# Revit family: 3000.123.6-124.6 Down Pipe Junction 100x100 SE
name_source: partatom
category: Plumbing Fixtures
units: mm (PartAtom-declared; Revit-internal decimal feet)

## family parameters
Always vertical = Yes
Cut with Voids When Loaded = No
OmniClass Number = 23.13.41.39
Part Type = Normal
Room Calculation Point = No
Round Connector Dimension = Use Diameter
Shared = No
Work Plane-Based = No

## types (2) — shared parameters
CW Connection = No
HW Connection = No
Manufacturer = Aquanight Industries Ltd
URL = www.aquaknight.co.nz
Vent Connection = No
Waste Connection = Yes
zero-valued in all types: Default Elevation

## per-type parameters (varying)
| type | Description | Model | Non-Vented | Vented |
| 3000.124.6 100x100 Vented Non-Vented | Down-Pipe Junction 100mm Inlet w 100mm Outlet Non-Vented Side Exit Big Flange | 3000.124.6 | Yes | No |
| 3000.123.6 100x100 Vented | Down-Pipe Junction 100mm Inlet w 100mm Outlet Vented Side Exit Big Flange | 3000.123.6 | No | Yes |

## geometry (parser evidence)
native form markers: Sweep x3
no freeform markers — native parametric forms only
